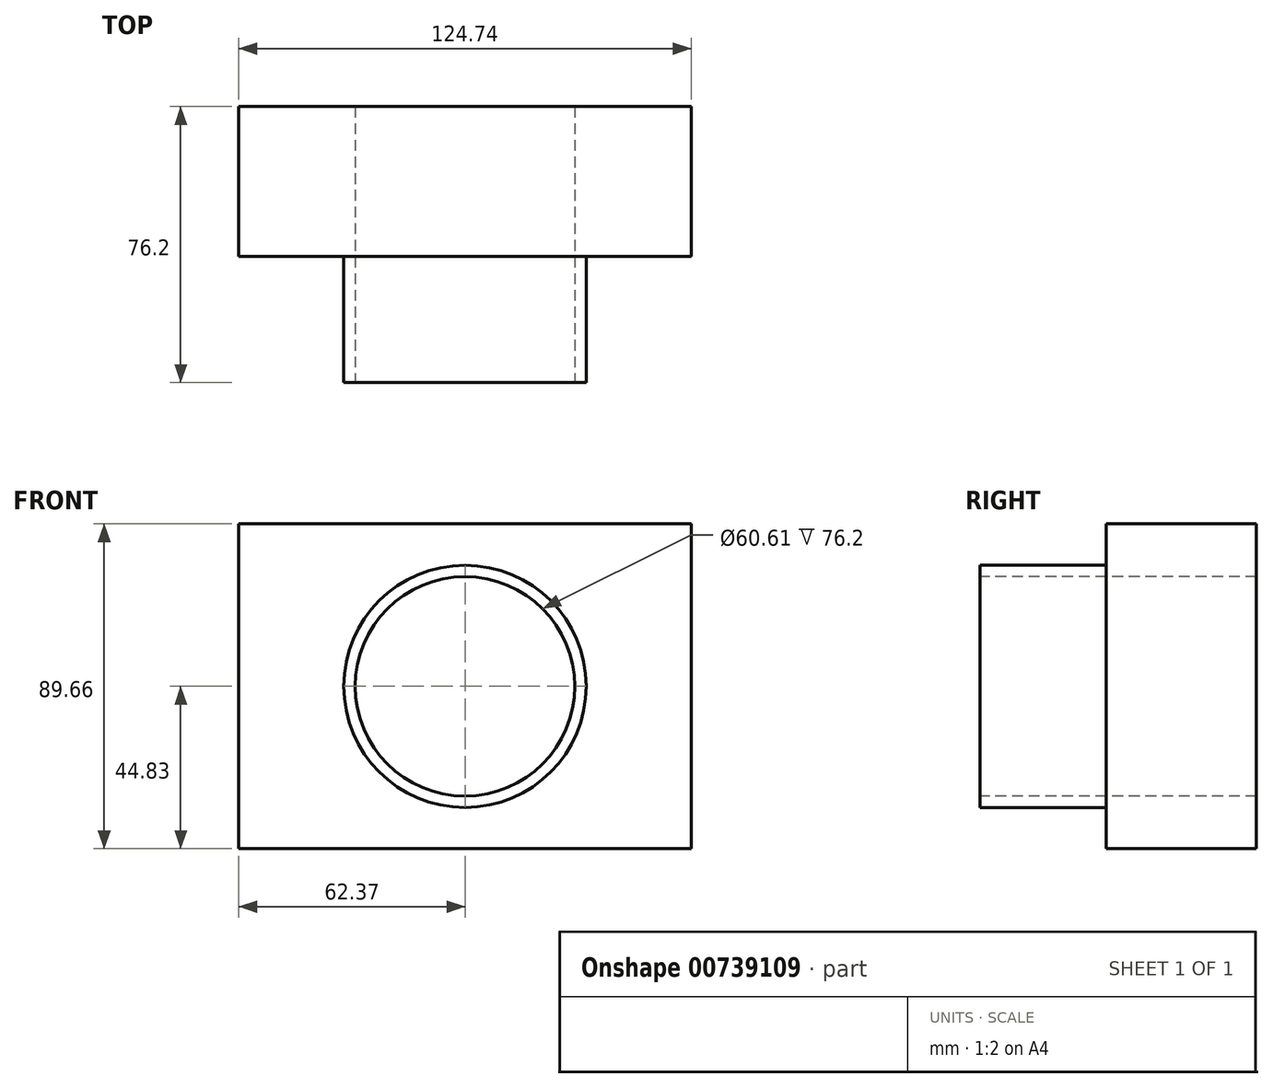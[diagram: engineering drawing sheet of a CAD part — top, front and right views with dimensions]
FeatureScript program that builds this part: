
annotation { "Feature Type Name" : "Feature", "Feature Type Description" : "" }
export const myFeature = defineFeature(function(context is Context, id is Id, definition is map)
    precondition{}
    {
        {
            var Q0;
            Q0=qCreatedBy(makeId("Front.planeOp"),FACE);
            var sketch = newSketch(context, id + "F0", { "sketchPlane" : qUnion([Q0])});
            skLineSegment(sketch, "E0.bottom", {"start": v(62.37, -44.83) * mm, "end": v(-62.37, -44.83) * mm});
            skLineSegment(sketch, "E0.top", {"start": v(62.37, 44.83) * mm, "end": v(-62.37, 44.83) * mm});
            skLineSegment(sketch, "E0.left", {"start": v(62.37, -44.83) * mm, "end": v(62.37, 44.83) * mm});
            skLineSegment(sketch, "E0.right", {"start": v(-62.37, -44.83) * mm, "end": v(-62.37, 44.83) * mm});
            skPoint(sketch, "E0.middle", {"position": v(0, 0) * mm});
            skSolve(sketch);
        }
        {
            var Q0;
            Q0 = qSketchRegion(id + "F0", true);
            extrude(context, id + "F1", {"entities" : qUnion([Q0]), "depth" : 41.4 * mm, "offsetDistance" : 25.4 * mm});
        }
        {
            var Q0;
            Q0=makeQuery(id+"F1.opExtrude","CAP_FACE",FACE,{"disambiguationData":[OSD([sQuery(id+"F0.wireOp",EDGE,"E0.bottom"),sQuery(id+"F0.wireOp",EDGE,"E0.top"),sQuery(id+"F0.wireOp",EDGE,"E0.left"),sQuery(id+"F0.wireOp",EDGE,"E0.right")])],"isStart":false});
            var sketch = newSketch(context, id + "F2", { "sketchPlane" : qUnion([Q0])});
            skCircle(sketch, "E1", {"center": v(0, 0) * mm, "radius": 33.43 * mm});
            skSolve(sketch);
        }
        {
            var Q0;
            Q0=makeQuery(id+"F2.imprint","IMPRINT",FACE,{"disambiguationData":[TD([[makeQuery(id+"F2.imprint","IMPRINT",EDGE,{"derivedFrom":sQuery(id+"F2.wireOp",EDGE,"E1")}),1.0]])]});
            extrude(context, id + "F3", {"entities" : qUnion([Q0]), "operationType" : NewBodyOperationType.ADD, "depth" : 34.8 * mm, "offsetDistance" : 25.4 * mm});
        }
        {
            var Q0;
            Q0=makeQuery(id+"F3.opExtrude","CAP_FACE",FACE,{"disambiguationData":[OSD([sQuery(id+"F2.wireOp",EDGE,"E1")])],"isStart":false});
            var sketch = newSketch(context, id + "F4", { "sketchPlane" : qUnion([Q0])});
            skCircle(sketch, "E2", {"center": v(0, 0) * mm, "radius": 30.3 * mm});
            skSolve(sketch);
        }
        {
            var Q0;
            Q0=makeQuery(id+"F4.imprint","IMPRINT",FACE,{"disambiguationData":[TD([[makeQuery(id+"F4.imprint","IMPRINT",EDGE,{"derivedFrom":sQuery(id+"F4.wireOp",EDGE,"E2")}),1.0]])]});
            extrude(context, id + "F5", {"entities" : qUnion([Q0]), "operationType" : NewBodyOperationType.REMOVE, "oppositeDirection" : true, "depth" : 96.27 * mm, "offsetDistance" : 25.4 * mm});
        }
    });
